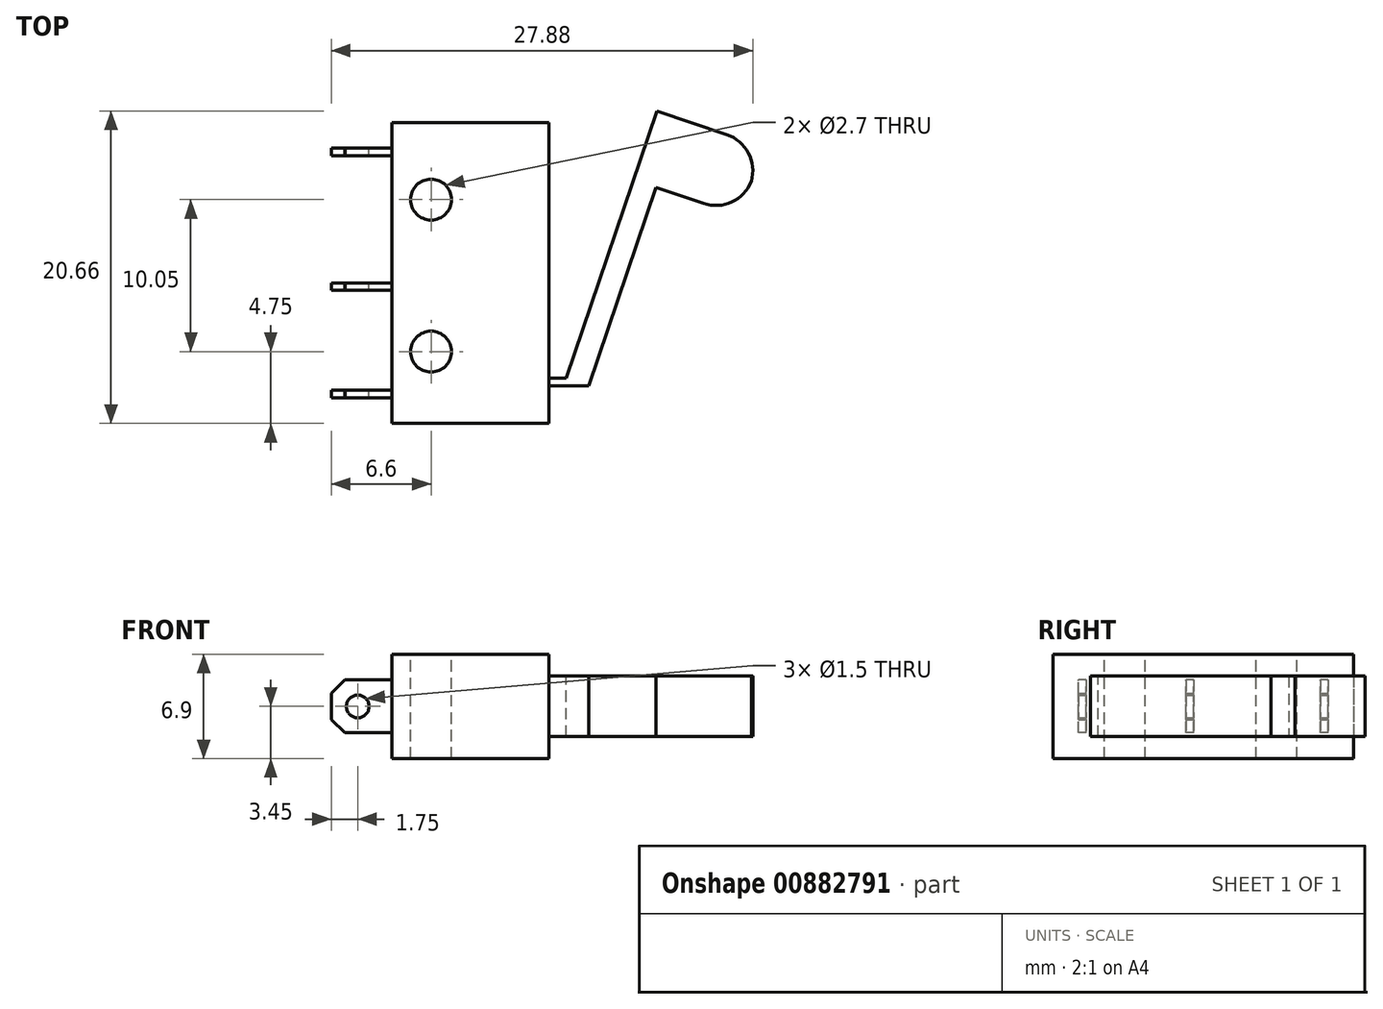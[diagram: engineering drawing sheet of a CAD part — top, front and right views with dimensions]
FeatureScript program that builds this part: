
annotation { "Feature Type Name" : "Feature", "Feature Type Description" : "" }
export const myFeature = defineFeature(function(context is Context, id is Id, definition is map)
    precondition{}
    {
        {
            var Q0;
            Q0=qCreatedBy(makeId("Top.planeOp"),FACE);
            var sketch = newSketch(context, id + "F0", { "sketchPlane" : qUnion([Q0])});
            skLineSegment(sketch, "E0.bottom", {"start": v(5.2, -9.95) * mm, "end": v(-5.2, -9.95) * mm});
            skLineSegment(sketch, "E0.top", {"start": v(5.2, 9.95) * mm, "end": v(-5.2, 9.95) * mm});
            skLineSegment(sketch, "E0.left", {"start": v(5.2, -9.95) * mm, "end": v(5.2, 9.95) * mm});
            skLineSegment(sketch, "E0.right", {"start": v(-5.2, -9.95) * mm, "end": v(-5.2, 9.95) * mm});
            skPoint(sketch, "E0.middle", {"position": v(0, 0) * mm});
            skSolve(sketch);
        }
        {
            var Q0;
            Q0 = qSketchRegion(id + "F0", true);
            extrude(context, id + "F1", {"entities" : qUnion([Q0]), "depth" : 6.9 * mm, "offsetDistance" : 25.4 * mm});
        }
        {
            var Q0;
            Q0=makeQuery(id+"F1.opExtrude","CAP_FACE",FACE,{"disambiguationData":[OSD([sQuery(id+"F0.wireOp",EDGE,"E0.bottom"),sQuery(id+"F0.wireOp",EDGE,"E0.top"),sQuery(id+"F0.wireOp",EDGE,"E0.left"),sQuery(id+"F0.wireOp",EDGE,"E0.right")])],"isStart":false});
            var sketch = newSketch(context, id + "F2", { "sketchPlane" : qUnion([Q0])});
            skCircle(sketch, "E1", {"center": v(-2.6, 4.85) * mm, "radius": 1.35 * mm});
            skCircle(sketch, "E2", {"center": v(-2.6, -5.2) * mm, "radius": 1.35 * mm});
            skSolve(sketch);
        }
        {
            var Q0;
            Q0 = qSketchRegion(id + "F2", true);
            var Q1;
            Q1=makeQuery(id+"F1.opExtrude","CAP_FACE",FACE,{"disambiguationData":[OSD([sQuery(id+"F0.wireOp",EDGE,"E0.bottom"),sQuery(id+"F0.wireOp",EDGE,"E0.top"),sQuery(id+"F0.wireOp",EDGE,"E0.left"),sQuery(id+"F0.wireOp",EDGE,"E0.right")])],"isStart":true});
            extrude(context, id + "F3", {"entities" : qUnion([Q0]), "operationType" : NewBodyOperationType.REMOVE, "endBound" : BoundingType.UP_TO_SURFACE, "oppositeDirection" : true, "depth" : 25.4 * mm, "endBoundEntityFace" : qUnion([Q1]), "offsetDistance" : 25.4 * mm});
        }
        {
            var Q0;
            Q0=makeQuery(id+"F1.opExtrude","SWEPT_FACE",FACE,{"disambiguationData":[OSD([sQuery(id+"F0.wireOp",EDGE,"E0.right")])]});
            var sketch = newSketch(context, id + "F4", { "sketchPlane" : qUnion([Q0])});
            skLineSegment(sketch, "E3.bottom", {"start": v(-8.25, 1.7) * mm, "end": v(-7.75, 1.7) * mm});
            skLineSegment(sketch, "E3.top", {"start": v(-8.25, 5.2) * mm, "end": v(-7.75, 5.2) * mm});
            skLineSegment(sketch, "E3.left", {"start": v(-8.25, 1.7) * mm, "end": v(-8.25, 5.2) * mm});
            skLineSegment(sketch, "E3.right", {"start": v(-7.75, 1.7) * mm, "end": v(-7.75, 5.2) * mm});
            skLineSegment(sketch, "E4.bottom", {"start": v(0.65, 1.7) * mm, "end": v(1.15, 1.7) * mm});
            skLineSegment(sketch, "E4.top", {"start": v(0.65, 5.2) * mm, "end": v(1.15, 5.2) * mm});
            skLineSegment(sketch, "E4.left", {"start": v(0.65, 1.7) * mm, "end": v(0.65, 5.2) * mm});
            skLineSegment(sketch, "E4.right", {"start": v(1.15, 1.7) * mm, "end": v(1.15, 5.2) * mm});
            skLineSegment(sketch, "E5.bottom", {"start": v(7.75, 1.7) * mm, "end": v(8.25, 1.7) * mm});
            skLineSegment(sketch, "E5.top", {"start": v(7.75, 5.2) * mm, "end": v(8.25, 5.2) * mm});
            skLineSegment(sketch, "E5.left", {"start": v(7.75, 1.7) * mm, "end": v(7.75, 5.2) * mm});
            skLineSegment(sketch, "E5.right", {"start": v(8.25, 1.7) * mm, "end": v(8.25, 5.2) * mm});
            skLineSegment(sketch, "E6", {"start": v(-9.95, 3.45) * mm, "end": v(9.95, 3.45) * mm});
            skSolve(sketch);
        }
        {
            var Q0;
            Q0 = qSketchRegion(id + "F4", true);
            extrude(context, id + "F5", {"entities" : qUnion([Q0]), "operationType" : NewBodyOperationType.ADD, "depth" : 4 * mm, "offsetDistance" : 25.4 * mm});
        }
        {
            var Q0;
            Q0=makeQuery(id+"F5.opExtrude","SWEPT_FACE",FACE,{"disambiguationData":[OSD([sQuery(id+"F4.wireOp",EDGE,"E3.left")])]});
            var sketch = newSketch(context, id + "F6", { "sketchPlane" : qUnion([Q0])});
            skCircle(sketch, "E7", {"center": v(7.45, 3.45) * mm, "radius": 0.75 * mm});
            skLineSegment(sketch, "E8", {"start": v(8.31, 5.2) * mm, "end": v(9.2, 4.3) * mm});
            skLineSegment(sketch, "E9", {"start": v(9.2, 2.6) * mm, "end": v(8.31, 1.7) * mm});
            skLineSegment(sketch, "E10", {"start": v(8.31, 1.7) * mm, "end": v(9.2, 1.7) * mm});
            skLineSegment(sketch, "E11", {"start": v(9.2, 1.7) * mm, "end": v(9.2, 2.6) * mm});
            skLineSegment(sketch, "E12", {"start": v(8.31, 5.2) * mm, "end": v(9.2, 5.2) * mm});
            skLineSegment(sketch, "E13", {"start": v(9.2, 5.2) * mm, "end": v(9.2, 4.3) * mm});
            skLineSegment(sketch, "E14", {"start": v(5.2, 3.45) * mm, "end": v(9.2, 3.45) * mm});
            skSolve(sketch);
        }
        {
            var Q0;
            Q0 = qSketchRegion(id + "F6", true);
            var Q1;
            Q1=makeQuery(id+"F5.opExtrude","SWEPT_FACE",FACE,{"disambiguationData":[OSD([sQuery(id+"F4.wireOp",EDGE,"E5.right")])]});
            extrude(context, id + "F7", {"entities" : qUnion([Q0]), "operationType" : NewBodyOperationType.REMOVE, "endBound" : BoundingType.UP_TO_SURFACE, "oppositeDirection" : true, "depth" : 25.4 * mm, "endBoundEntityFace" : qUnion([Q1]), "offsetDistance" : 25.4 * mm});
        }
        {
            var Q0;
            Q0=makeQuery(id+"F1.opExtrude","SWEPT_FACE",FACE,{"disambiguationData":[OSD([sQuery(id+"F0.wireOp",EDGE,"E0.left")])]});
            var sketch = newSketch(context, id + "F8", { "sketchPlane" : qUnion([Q0])});
            skLineSegment(sketch, "E15.bottom", {"start": v(-6.95, 1.45) * mm, "end": v(-7.45, 1.45) * mm});
            skLineSegment(sketch, "E15.top", {"start": v(-6.95, 5.45) * mm, "end": v(-7.45, 5.45) * mm});
            skLineSegment(sketch, "E15.left", {"start": v(-6.95, 1.45) * mm, "end": v(-6.95, 5.45) * mm});
            skLineSegment(sketch, "E15.right", {"start": v(-7.45, 1.45) * mm, "end": v(-7.45, 5.45) * mm});
            skLineSegment(sketch, "E16", {"start": v(-9.95, 3.45) * mm, "end": v(9.95, 3.45) * mm});
            skSolve(sketch);
        }
        {
            var Q0;
            Q0 = qSketchRegion(id + "F8", true);
            extrude(context, id + "F9", {"entities" : qUnion([Q0]), "operationType" : NewBodyOperationType.ADD, "depth" : 1.15 * mm, "offsetDistance" : 25.4 * mm});
        }
        {
            var Q0;
            Q0=makeQuery(id+"F9.opExtrude","SWEPT_FACE",FACE,{"disambiguationData":[OSD([sQuery(id+"F8.wireOp",EDGE,"E15.bottom")])]});
            var sketch = newSketch(context, id + "F10", { "sketchPlane" : qUnion([Q0])});
            skLineSegment(sketch, "E17", {"start": v(6.35, 6.95) * mm, "end": v(6.35, 7.45) * mm});
            skLineSegment(sketch, "E18", {"start": v(6.35, 7.45) * mm, "end": v(7.82, 7.45) * mm});
            skLineSegment(sketch, "E19", {"start": v(7.82, 7.45) * mm, "end": v(6.35, 6.95) * mm});
            skSolve(sketch);
        }
        {
            var Q0;
            Q0 = qSketchRegion(id + "F10", true);
            var Q1;
            Q1=makeQuery(id+"F9.opExtrude","SWEPT_FACE",FACE,{"disambiguationData":[OSD([sQuery(id+"F8.wireOp",EDGE,"E15.top")])]});
            extrude(context, id + "F11", {"entities" : qUnion([Q0]), "operationType" : NewBodyOperationType.ADD, "endBound" : BoundingType.UP_TO_SURFACE, "oppositeDirection" : true, "depth" : 25.4 * mm, "endBoundEntityFace" : qUnion([Q1]), "offsetDistance" : 25.4 * mm});
        }
        {
            var Q0;
            Q0=makeQuery(id+"F11.opExtrude","SWEPT_FACE",FACE,{"disambiguationData":[OSD([sQuery(id+"F10.wireOp",EDGE,"E19")])]});
            var sketch = newSketch(context, id + "F12", { "sketchPlane" : qUnion([Q0])});
            skLineSegment(sketch, "E20.bottom", {"start": v(-9.8, 1.45) * mm, "end": v(-8.25, 1.45) * mm});
            skLineSegment(sketch, "E20.top", {"start": v(-9.8, 5.45) * mm, "end": v(-8.25, 5.45) * mm});
            skLineSegment(sketch, "E20.left", {"start": v(-9.8, 1.45) * mm, "end": v(-9.8, 5.45) * mm});
            skLineSegment(sketch, "E20.right", {"start": v(-8.25, 1.45) * mm, "end": v(-8.25, 5.45) * mm});
            skSolve(sketch);
        }
        {
            var Q0;
            Q0 = qSketchRegion(id + "F12", true);
            extrude(context, id + "F13", {"entities" : qUnion([Q0]), "operationType" : NewBodyOperationType.ADD, "depth" : 18.65 * mm, "offsetDistance" : 25.4 * mm});
        }
        {
            var Q0;
            Q0=makeQuery(id+"F13.opExtrude","SWEPT_FACE",FACE,{"disambiguationData":[OSD([sQuery(id+"F12.wireOp",EDGE,"E20.left")])]});
            var sketch = newSketch(context, id + "F14", { "sketchPlane" : qUnion([Q0])});
            skLineSegment(sketch, "E21.bottom", {"start": v(14.11, 5.45) * mm, "end": v(9.31, 5.45) * mm});
            skLineSegment(sketch, "E21.top", {"start": v(14.11, 1.45) * mm, "end": v(9.31, 1.45) * mm});
            skLineSegment(sketch, "E21.left", {"start": v(14.11, 5.45) * mm, "end": v(14.11, 1.45) * mm});
            skLineSegment(sketch, "E21.right", {"start": v(9.31, 5.45) * mm, "end": v(9.31, 1.45) * mm});
            skSolve(sketch);
        }
        {
            var Q0;
            Q0 = qSketchRegion(id + "F14", true);
            extrude(context, id + "F15", {"entities" : qUnion([Q0]), "operationType" : NewBodyOperationType.ADD, "depth" : 5.85 * mm, "offsetDistance" : 25.4 * mm});
        }
        {
            var Q0;
            Q0=makeQuery(id+"F15.opExtrude","CAP_EDGE",EDGE,{"disambiguationData":[OSD([sQuery(id+"F14.wireOp",EDGE,"E21.left")])],"isStart":false});
            var Q1;
            Q1=makeQuery(id+"F15.opExtrude","CAP_EDGE",EDGE,{"disambiguationData":[OSD([sQuery(id+"F14.wireOp",EDGE,"E21.right")])],"isStart":false});
            fillet(context, id + "F16", {"entities" : qUnion([Q0, Q1]), "radius" : 2.54 * mm, "tangentPropagation" : true, "allowEdgeOverflow" : false});
        }
    });
